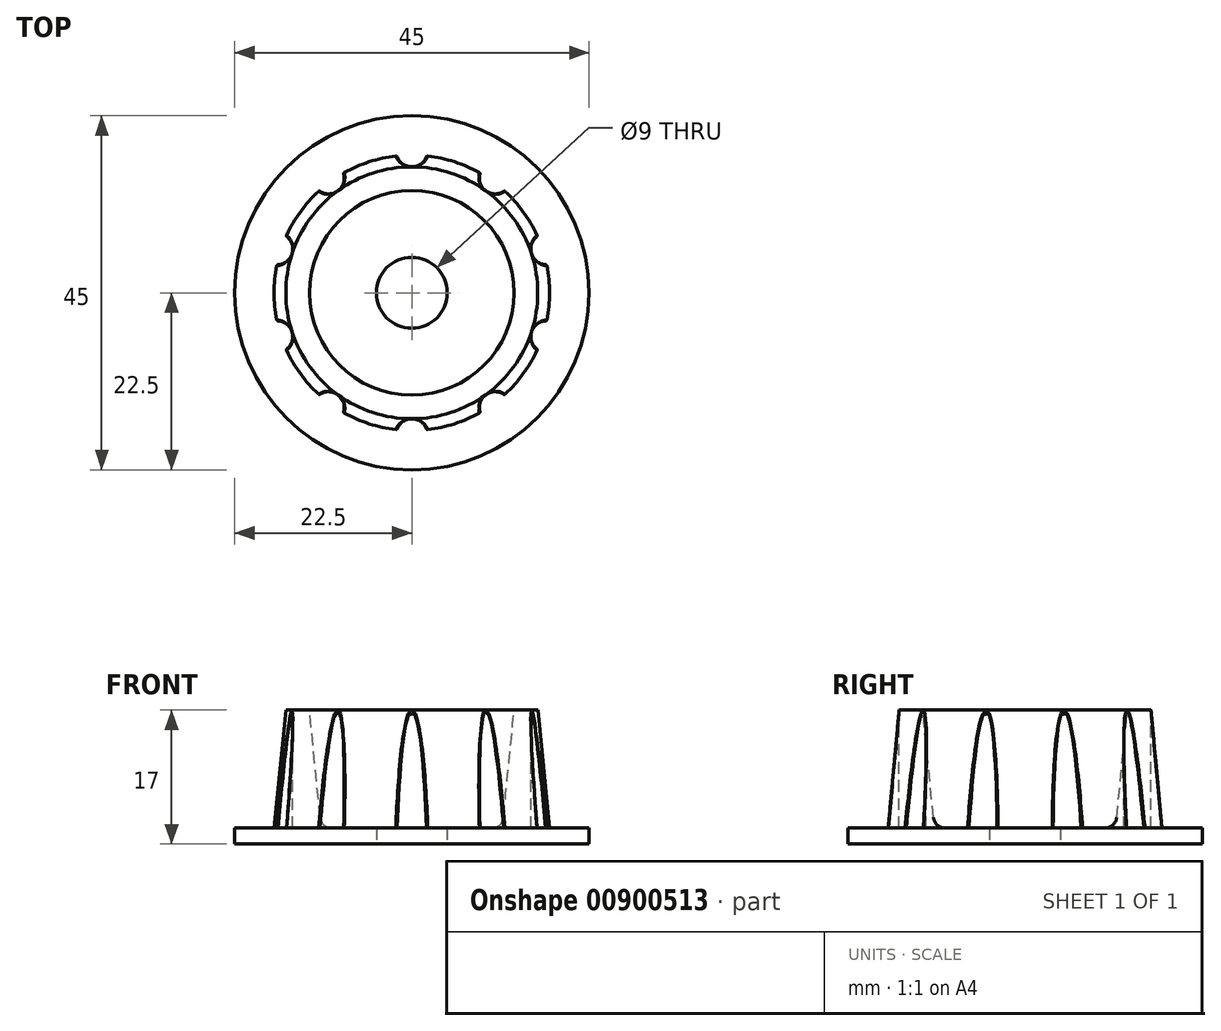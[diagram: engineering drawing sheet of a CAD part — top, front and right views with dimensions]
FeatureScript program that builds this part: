
annotation { "Feature Type Name" : "Feature", "Feature Type Description" : "" }
export const myFeature = defineFeature(function(context is Context, id is Id, definition is map)
    precondition{}
    {
        {
            var Q0;
            Q0=qCreatedBy(makeId("Top.planeOp"),FACE);
            var sketch = newSketch(context, id + "F0", { "sketchPlane" : qUnion([Q0])});
            skLineSegment(sketch, "E0.bottom", {"start": v(0, 44.5) * mm, "end": v(43.4, 44.5) * mm});
            skLineSegment(sketch, "E0.top", {"start": v(0, 0) * mm, "end": v(43.4, 0) * mm});
            skLineSegment(sketch, "E0.left", {"start": v(0, 44.5) * mm, "end": v(0, 0) * mm});
            skLineSegment(sketch, "E0.right", {"start": v(43.4, 44.5) * mm, "end": v(43.4, 0) * mm});
            skCircle(sketch, "E1", {"center": v(29.4, 27) * mm, "radius": 4.5 * mm});
            skSolve(sketch);
        }
        {
            var Q0;
            Q0=makeQuery(id+"F0.imprint","IMPRINT",FACE,{"disambiguationData":[TD([[makeQuery(id+"F0.imprint","IMPRINT",EDGE,{"derivedFrom":sQuery(id+"F0.wireOp",EDGE,"E0.bottom")}),-1.0]])]});
            var sketch = newSketch(context, id + "F1", { "sketchPlane" : qUnion([Q0])});
            skCircle(sketch, "E2", {"center": v(29.4, 27) * mm, "radius": 4.5 * mm});
            skCircle(sketch, "E3", {"center": v(29.4, 27) * mm, "radius": 22.5 * mm});
            skSolve(sketch);
        }
        {
            var Q0;
            Q0 = qSketchRegion(id + "F1", true);
            extrude(context, id + "F2", {"entities" : qUnion([Q0]), "depth" : 2 * mm, "offsetDistance" : 25 * mm});
        }
        {
            var Q0;
            Q0=makeQuery(id+"F2.opExtrude","CAP_FACE",FACE,{"disambiguationData":[OSD([sQuery(id+"F1.wireOp",EDGE,"E2"),sQuery(id+"F1.wireOp",EDGE,"E3")])],"isStart":false});
            var sketch = newSketch(context, id + "F3", { "sketchPlane" : qUnion([Q0])});
            skCircle(sketch, "E4", {"center": v(29.4, 27) * mm, "radius": 11.5 * mm});
            skCircle(sketch, "E5", {"center": v(29.4, 27) * mm, "radius": 17.5 * mm});
            skSolve(sketch);
        }
        {
            var Q0;
            Q0 = qSketchRegion(id + "F3", true);
            extrude(context, id + "F4", {"entities" : qUnion([Q0]), "operationType" : NewBodyOperationType.ADD, "depth" : 15 * mm, "offsetDistance" : 25 * mm});
        }
        {
            var Q0;
            Q0=makeQuery(id+"F4.opExtrude","CAP_EDGE",EDGE,{"disambiguationData":[OSD([sQuery(id+"F3.wireOp",EDGE,"E4")])],"isStart":false});
            var Q1;
            Q1=makeQuery(id+"F4.opExtrude","CAP_EDGE",EDGE,{"disambiguationData":[OSD([sQuery(id+"F3.wireOp",EDGE,"E5")])],"isStart":false});
            chamfer(context, id + "F5", {"entities" : qUnion([Q0, Q1]), "chamferType" : ChamferType.TWO_OFFSETS, "width1" : 15 * mm, "oppositeDirection" : false, "width2" : 1.5 * mm, "tangentPropagation" : true});
        }
        {
            var Q0;
            Q0=makeQuery(id+"F4.opExtrude","CAP_FACE",FACE,{"disambiguationData":[OSD([sQuery(id+"F3.wireOp",EDGE,"E4"),sQuery(id+"F3.wireOp",EDGE,"E5")])],"isStart":false});
            var sketch = newSketch(context, id + "F6", { "sketchPlane" : qUnion([Q0])});
            skCircle(sketch, "E6", {"center": v(29.4, 45) * mm, "radius": 2 * mm});
            skCircle(sketch, "E7.1.0", {"center": v(18.82, 41.56) * mm, "radius": 2 * mm});
            skCircle(sketch, "E7.2.0", {"center": v(12.28, 32.56) * mm, "radius": 2 * mm});
            skCircle(sketch, "E7.3.0", {"center": v(12.28, 21.44) * mm, "radius": 2 * mm});
            skCircle(sketch, "E7.4.0", {"center": v(18.82, 12.44) * mm, "radius": 2 * mm});
            skCircle(sketch, "E7.5.0", {"center": v(29.4, 9) * mm, "radius": 2 * mm});
            skCircle(sketch, "E7.6.0", {"center": v(39.98, 12.44) * mm, "radius": 2 * mm});
            skCircle(sketch, "E7.7.0", {"center": v(46.52, 21.44) * mm, "radius": 2 * mm});
            skCircle(sketch, "E7.8.0", {"center": v(46.52, 32.56) * mm, "radius": 2 * mm});
            skCircle(sketch, "E7.9.0", {"center": v(39.98, 41.56) * mm, "radius": 2 * mm});
            skPoint(sketch, "E7.center", {"position": v(29.4, 27) * mm});
            skSolve(sketch);
        }
        {
            var Q0;
            Q0 = qSketchRegion(id + "F6", true);
            var Q1;
            {var subQ0=sQuery(id+"F1.wireOp",EDGE,"E3");Q1=makeQuery(id+"F4.boolean.opBoolean","SPLIT",FACE,{"disambiguationData":[TD([makeQuery(id+"F2.opExtrude","SWEPT_FACE",FACE,{"disambiguationData":[OSD([subQ0])]})])],"derivedFrom":makeQuery(id+"F2.opExtrude","CAP_FACE",FACE,{"disambiguationData":[OSD([sQuery(id+"F1.wireOp",EDGE,"E2"),subQ0])],"isStart":false})});}
            extrude(context, id + "F7", {"entities" : qUnion([Q0]), "operationType" : NewBodyOperationType.REMOVE, "endBound" : BoundingType.UP_TO_SURFACE, "oppositeDirection" : true, "depth" : 25 * mm, "endBoundEntityFace" : qUnion([Q1]), "offsetDistance" : 25 * mm});
        }
        {
            var Q0;
            Q0=makeQuery(id+"F7.boolean.opBoolean","INTERSECT",EDGE,{"disambiguationData":[OD(0.0)],"derivedFrom":[makeQuery(id+"F5.opChamfer","BLEND_FACE",FACE,{"disambiguationData":[OSD([sQuery(id+"F3.wireOp",EDGE,"E5")])]}),makeQuery(id+"F7.opExtrude","SWEPT_FACE",FACE,{"disambiguationData":[OSD([sQuery(id+"F6.wireOp",EDGE,"E7.1.0")])]})]});
            var Q1;
            Q1=makeQuery(id+"F7.boolean.opBoolean","INTERSECT",EDGE,{"disambiguationData":[OD(0.0)],"derivedFrom":[makeQuery(id+"F5.opChamfer","BLEND_FACE",FACE,{"disambiguationData":[OSD([sQuery(id+"F3.wireOp",EDGE,"E5")])]}),makeQuery(id+"F7.opExtrude","SWEPT_FACE",FACE,{"disambiguationData":[OSD([sQuery(id+"F6.wireOp",EDGE,"E6")])]})]});
            var Q2;
            Q2=makeQuery(id+"F7.boolean.opBoolean","INTERSECT",EDGE,{"disambiguationData":[OD(0.0)],"derivedFrom":[makeQuery(id+"F5.opChamfer","BLEND_FACE",FACE,{"disambiguationData":[OSD([sQuery(id+"F3.wireOp",EDGE,"E5")])]}),makeQuery(id+"F7.opExtrude","SWEPT_FACE",FACE,{"disambiguationData":[OSD([sQuery(id+"F6.wireOp",EDGE,"E7.9.0")])]})]});
            var Q3;
            Q3=makeQuery(id+"F7.boolean.opBoolean","INTERSECT",EDGE,{"disambiguationData":[OD(1.0)],"derivedFrom":[makeQuery(id+"F5.opChamfer","BLEND_FACE",FACE,{"disambiguationData":[OSD([sQuery(id+"F3.wireOp",EDGE,"E5")])]}),makeQuery(id+"F7.opExtrude","SWEPT_FACE",FACE,{"disambiguationData":[OSD([sQuery(id+"F6.wireOp",EDGE,"E7.8.0")])]})]});
            var Q4;
            Q4=makeQuery(id+"F7.boolean.opBoolean","INTERSECT",EDGE,{"disambiguationData":[OD(1.0)],"derivedFrom":[makeQuery(id+"F5.opChamfer","BLEND_FACE",FACE,{"disambiguationData":[OSD([sQuery(id+"F3.wireOp",EDGE,"E5")])]}),makeQuery(id+"F7.opExtrude","SWEPT_FACE",FACE,{"disambiguationData":[OSD([sQuery(id+"F6.wireOp",EDGE,"E7.7.0")])]})]});
            var Q5;
            Q5=makeQuery(id+"F7.boolean.opBoolean","INTERSECT",EDGE,{"disambiguationData":[OD(1.0)],"derivedFrom":[makeQuery(id+"F5.opChamfer","BLEND_FACE",FACE,{"disambiguationData":[OSD([sQuery(id+"F3.wireOp",EDGE,"E5")])]}),makeQuery(id+"F7.opExtrude","SWEPT_FACE",FACE,{"disambiguationData":[OSD([sQuery(id+"F6.wireOp",EDGE,"E7.6.0")])]})]});
            var Q6;
            Q6=makeQuery(id+"F7.boolean.opBoolean","INTERSECT",EDGE,{"disambiguationData":[OD(1.0)],"derivedFrom":[makeQuery(id+"F5.opChamfer","BLEND_FACE",FACE,{"disambiguationData":[OSD([sQuery(id+"F3.wireOp",EDGE,"E5")])]}),makeQuery(id+"F7.opExtrude","SWEPT_FACE",FACE,{"disambiguationData":[OSD([sQuery(id+"F6.wireOp",EDGE,"E7.5.0")])]})]});
            var Q7;
            Q7=makeQuery(id+"F7.boolean.opBoolean","INTERSECT",EDGE,{"disambiguationData":[OD(1.0)],"derivedFrom":[makeQuery(id+"F5.opChamfer","BLEND_FACE",FACE,{"disambiguationData":[OSD([sQuery(id+"F3.wireOp",EDGE,"E5")])]}),makeQuery(id+"F7.opExtrude","SWEPT_FACE",FACE,{"disambiguationData":[OSD([sQuery(id+"F6.wireOp",EDGE,"E7.2.0")])]})]});
            var Q8;
            Q8=makeQuery(id+"F7.boolean.opBoolean","INTERSECT",EDGE,{"disambiguationData":[OD(0.0)],"derivedFrom":[makeQuery(id+"F5.opChamfer","BLEND_FACE",FACE,{"disambiguationData":[OSD([sQuery(id+"F3.wireOp",EDGE,"E5")])]}),makeQuery(id+"F7.opExtrude","SWEPT_FACE",FACE,{"disambiguationData":[OSD([sQuery(id+"F6.wireOp",EDGE,"E7.3.0")])]})]});
            var Q9;
            Q9=makeQuery(id+"F7.boolean.opBoolean","INTERSECT",EDGE,{"disambiguationData":[OD(0.0)],"derivedFrom":[makeQuery(id+"F5.opChamfer","BLEND_FACE",FACE,{"disambiguationData":[OSD([sQuery(id+"F3.wireOp",EDGE,"E5")])]}),makeQuery(id+"F7.opExtrude","SWEPT_FACE",FACE,{"disambiguationData":[OSD([sQuery(id+"F6.wireOp",EDGE,"E7.4.0")])]})]});
            fillet(context, id + "F8", {"entities" : qUnion([Q0, Q1, Q2, Q3, Q4, Q5, Q6, Q7, Q8, Q9]), "radius" : 0.15 * mm, "tangentPropagation" : true, "allowEdgeOverflow" : false});
        }
        {
            var Q0;
            {var subQ0=sQuery(id+"F1.wireOp",EDGE,"E2");var subQ1=sQuery(id+"F3.wireOp",EDGE,"E4");Q0=makeQuery(id+"F5.opChamfer","BLEND_EDGE",EDGE,{"blendedFrom":[makeQuery(id+"F4.opExtrude","CAP_EDGE",EDGE,{"disambiguationData":[OSD([subQ1])],"isStart":false}),makeQuery(id+"F4.boolean.opBoolean","SPLIT",FACE,{"disambiguationData":[TD([makeQuery(id+"F2.opExtrude","SWEPT_FACE",FACE,{"disambiguationData":[OSD([subQ0])]})])],"derivedFrom":makeQuery(id+"F2.opExtrude","CAP_FACE",FACE,{"disambiguationData":[OSD([subQ0,sQuery(id+"F1.wireOp",EDGE,"E3")])],"isStart":false})})],"blendedInto":[makeQuery(id+"F4.boolean.opBoolean","SPLIT",FACE,{"disambiguationData":[TD([makeQuery(id+"F2.opExtrude","SWEPT_FACE",FACE,{"disambiguationData":[OSD([subQ0])]})])],"derivedFrom":makeQuery(id+"F2.opExtrude","CAP_FACE",FACE,{"disambiguationData":[OSD([subQ0,sQuery(id+"F1.wireOp",EDGE,"E3")])],"isStart":false})})]});}
            fillet(context, id + "F9", {"entities" : qUnion([Q0]), "radius" : 1.5 * mm, "tangentPropagation" : true, "allowEdgeOverflow" : false});
        }
    });
